# Revit family: Zumtobel MIRL mini
name_source: partatom
category: Leuchten
revit_build: Autodesk Revit 2016 (Build: 20150714_1515(x64)
units: mm (PartAtom-declared; Revit-internal decimal feet)

## family parameters
Basisbauteil = Fläche
Beim Laden mit Abzugskörper schneiden = Nein
Bemaßung runder Anschluss = Durchmesser verwenden
Gemeinsam genutzt = Nein
Lichtquelle = Ja
OmniClass-Nummer = 23.80.70.11
OmniClass-Titel = Luminaries for Internal Lighting
Raumberechnungspunkt = Nein
Teiletyp = Normal

## types (1)
- MIRL MINI LED1200
    Baugruppenkennzeichen = D5020200
    Beschreibung = Recessed LED luminaire
    Datei für fotometrisches Netz = 42184006_(STD).IES
    Emissionsform beim Rendern sichtbar = Nein
    Farbfilter = 16777215
    Farbtemperaturverschiebung bei Dämpfen der Lampe = <Keine Auswahl>
    Height = 38 mm  [stored 0.124672 ft]
    Hersteller = Zumtobel Lighting
    Lampe = LED
    Length = 170 mm  [stored 0.557743 ft]
    Modell = 42184007
    Neigungswinkel = 90.00°
    Scheinlast = 10 VA
    URL = http://www.zumtobel.com
    Voltage = 230 V
    Von Breite des Rechtecks ausssenden = 188 mm  [stored 0.616798 ft]
    Von Länge des Rechtecks aussenden = 188 mm  [stored 0.616798 ft]
    Vorgabe-Ansicht = 0 mm  [stored 0 ft]
    Width = 170 mm  [stored 0.557743 ft]

note: [stored X ft] marks values corroborated as IEEE doubles in the binary element streams (Revit-internal decimal feet)

## geometry (parser evidence)
native form markers: Sweep x3
no freeform markers — native parametric forms only
